# Revit family: Downflow_Unit_Heaters-QMark-MUH
name_source: partatom
category: Mechanical Equipment
revit_build: Autodesk Revit MEP 2012 (Build: 20110309_2315(x64)
units: mm (PartAtom-declared; Revit-internal decimal feet)

## types (1)
- Not a Type - Load Type Catalog
    Actual Supply Air Flow = 350 CFM
    Amps = 15 A
    Apparent Load = 3016 VA
    Bracket Location = 1' - 0 1/16"
    Bracket Position = 0' - 3 1/4"
    Casing = Paint - QMark - Black
    Control Volt = 208 V
    DT = 27 °F
    Default Elevation = 4' - 0"
    Depth = 0' - 8 1/2"
    Description = Horizontal / Downflow Unit Heaters
    FPM = 800' - 0"
    Fan Motor HP = 1/100
    Fan Motor RPM = 1600
    Fan Motor Volts = 208 V
    Frequency = 60 Hz
    Full Load Current = 15 A
    Height = 1' - 4"
    KW = 3000 W
    Length 1 = 1' - 2"
    Manufacturer = Marley Engineered Products
    Model = MUH
    Number of Poles = 1
    Phase = 1
    Power Factor = 1
    Product Documentation Link = http://www.marleymep.com
    Product Name = MUH - Horizontal / Downflow Unit Heaters
    Product Page URL = http://www.marleymep.com
    Supply Fan Motor Speed = 1600
    Total Heating Capacity = 10.2 Btu/h
    URL = http://www.marleymep.com
    Voltage = 208 V
    Watts = 32292 A
    Width = 1' - 2"
    Wire Size = 12

## geometry (parser evidence)
native form markers: Blend x8, Sweep x7
no freeform markers — native parametric forms only
